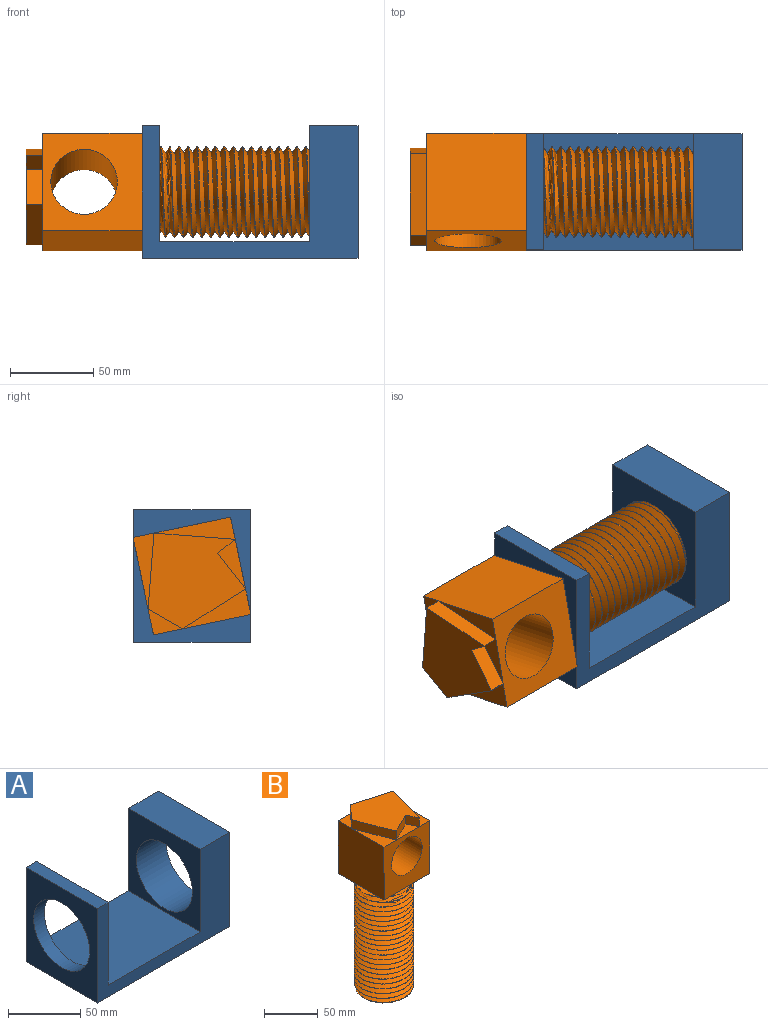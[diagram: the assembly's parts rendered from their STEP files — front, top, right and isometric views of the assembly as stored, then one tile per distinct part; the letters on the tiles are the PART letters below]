
ASSEMBLY  parts=2 mates=1
PART A: 12 faces, bbox 130x70x80 mm
  f0: plane 70x10.53mm, normal (0,0,1), area 737.3mm2, adj f1,f7,f8,f9
  f1: plane 80x70mm, normal (-1,0,0), area 3224.2mm2, adj f0,f2,f8,f9,f10
  f2: plane 130x70mm, normal (0,0,-1), area 9100mm2, adj f1,f3,f8,f9
  f3: plane 80x70mm, normal (1,0,0), area 3224.2mm2, adj f2,f4,f8,f9,f11
  f4: plane 70x29.32mm, normal (0,0,1), area 2052.7mm2, adj f3,f5,f8,f9
  f5: plane 70x70mm, normal (-1,0,0), area 2524.2mm2, adj f4,f6,f8,f9,f11
  f6: plane 90.14x70mm, normal (0,0,1), area 6310mm2, adj f5,f7,f8,f9
  f7: plane 70x70mm, normal (1,0,0), area 2524.2mm2, adj f0,f6,f8,f9,f10
  f8: plane 130x80mm, normal (0,-1,0), area 4090mm2, adj f0,f1,f2,f3,f4,f5,f6,f7
  f9: plane 130x80mm, normal (0,1,0), area 4090mm2, adj f0,f1,f2,f3,f4,f5,f6,f7
  f10: cylinder r=27.5mm len=55mm, axis (1,0,0), area 1820mm2, adj f1,f7
  f11: cylinder r=27.5mm len=55mm, axis (1,0,0), area 5066.9mm2, adj f3,f5
PART B: 28 faces, bbox 60x68.6x202.2 mm
  f0: plane 60x60mm, normal (1,0,0), area 3600mm2, adj f1,f6,f7,f19,f25
  f1: plane 70x60mm, normal (0,-1,0), area 2346.3mm2, adj f0,f4,f5,f6,f8,f16,f17,f20
  f2: cylinder r=27.5mm len=115mm, axis (0,0,1), area 2023.9mm2, adj f9,f11,f12,f13,f26
  f3: plane 45x45mm, normal (0,0,-1), area 1590.4mm2, adj f26
  f4: plane 60x60mm, normal (0,0,1), area 2336.7mm2, adj f1,f15,f16,f18,f20,f22,f24
  f5: plane 60x60mm, normal (-1,0,0), area 3600mm2, adj f1,f6,f7,f21,f23
  f6: plane 60x60mm, normal (0,0,-1), area 2343.4mm2, adj f0,f1,f5,f7,f14
  f7: plane 60x60mm, normal (0,1,0), area 2343.4mm2, adj f0,f5,f6,f8,f19,f23
  f8: cylinder r=20mm len=60mm, axis (0,-1,0), area 7539.8mm2, adj f1,f7
  f9: plane 52.83x51.34mm, normal (0,0,1), area 834.8mm2, adj f2,f11,f12,f13,f14
  f10: plane 1.77x1.32mm, normal (0,1,0), area 0.4mm2, adj f12,f13,f27
  f11: plane 1.54x1.01mm, normal (0,-1,0), area 0.8mm2, adj f2,f9,f13
  f12: bspline ~122.86x68.55mm, area 16202.5mm2, adj f2,f9,f10,f13,f26,f27
  f13: bspline ~123.77x68.55mm, area 16398.1mm2, adj f2,f9,f10,f11,f12,f26,f27
  f14: torus R=20mm, axis (0,0,1), area 1659.8mm2, adj f6,f9
  f15: plane 12.06x10mm, normal (-0.89,-0.45,0), area 134.8mm2, adj f4,f16,f17,f24
  f16: plane 24.17x12.06mm, normal (0.45,-0.89,0), area 270.1mm2, adj f1,f4,f15,f17
  f17: plane 30.18x12.06mm, normal (0,0,1), area 182mm2, adj f1,f15,f16
  f18: plane 44.15x12.84mm, normal (0.28,0.96,0), area 459.8mm2, adj f4,f19,f22,f24
  f19: plane 44.15x12.84mm, normal (0,0,1), area 283.4mm2, adj f0,f7,f18
  f20: plane 42.06x15.81mm, normal (-0.94,-0.35,0), area 449.3mm2, adj f1,f4,f21,f22
  f21: plane 42.06x15.81mm, normal (0,0,1), area 332.4mm2, adj f1,f5,f20
  f22: plane 17.94x15.85mm, normal (-0.75,0.66,0), area 239.4mm2, adj f4,f18,f20,f23
  f23: plane 17.94x15.85mm, normal (0,0,1), area 142.2mm2, adj f5,f7,f22
  f24: plane 47.16x13.71mm, normal (0.96,-0.28,0), area 491.2mm2, adj f4,f15,f18,f25
  f25: plane 47.16x13.71mm, normal (0,0,1), area 323.4mm2, adj f0,f1,f24
  f26: torus R=22.5mm, axis (0,0,-1), area 768.9mm2, adj f2,f3,f12,f13,f27
  f27: bspline ~5.19x4.13mm, area 14.7mm2, adj f10,f12,f13,f26
PLACE A t=(166.42,-23.55,-17.81)mm fixed
PLACE B rot(axis=(-0.1,-0.99,0.1),90.6deg) t=(166.42,-35.31,-13.31)mm
MATE revolute B.f2 <-> A.f10  axis (1,0,0) through (166.42,-58.55,22.19)mm
